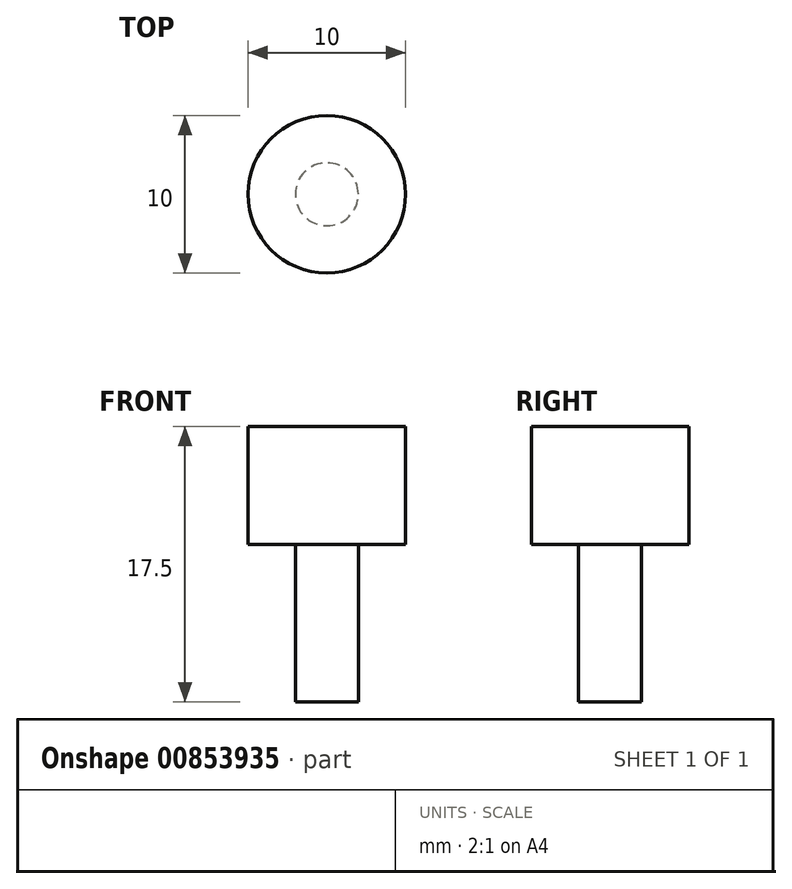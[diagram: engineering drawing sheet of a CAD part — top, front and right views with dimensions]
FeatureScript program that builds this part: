
annotation { "Feature Type Name" : "Feature", "Feature Type Description" : "" }
export const myFeature = defineFeature(function(context is Context, id is Id, definition is map)
    precondition{}
    {
        {
            var Q0;
            Q0=qCreatedBy(makeId("Top.planeOp"),FACE);
            var sketch = newSketch(context, id + "F0", { "sketchPlane" : qUnion([Q0])});
            skCircle(sketch, "E0", {"center": v(0, 0) * mm, "radius": 2 * mm});
            skCircle(sketch, "E1", {"center": v(0, 0) * mm, "radius": 5 * mm});
            skSolve(sketch);
        }
        {
            var Q0;
            Q0=makeQuery(id+"F0.imprint","IMPRINT",FACE,{"disambiguationData":[TD([[makeQuery(id+"F0.imprint","IMPRINT",EDGE,{"derivedFrom":sQuery(id+"F0.wireOp",EDGE,"E0")}),1.0]])]});
            extrude(context, id + "F1", {"entities" : qUnion([Q0]), "oppositeDirection" : true, "depth" : 10 * mm, "offsetDistance" : 25 * mm});
        }
        {
            var Q0;
            Q0 = qSketchRegion(id + "F0", true);
            var Q1;
            Q1=makeQuery(id+"F1.opExtrude","CAP_FACE",FACE,{"disambiguationData":[OSD([sQuery(id+"F0.wireOp",EDGE,"E0")])],"isStart":true});
            extrude(context, id + "F2", {"entities" : qUnion([Q0, Q1]), "operationType" : NewBodyOperationType.ADD, "depth" : 7.5 * mm, "offsetDistance" : 25 * mm});
        }
    });
